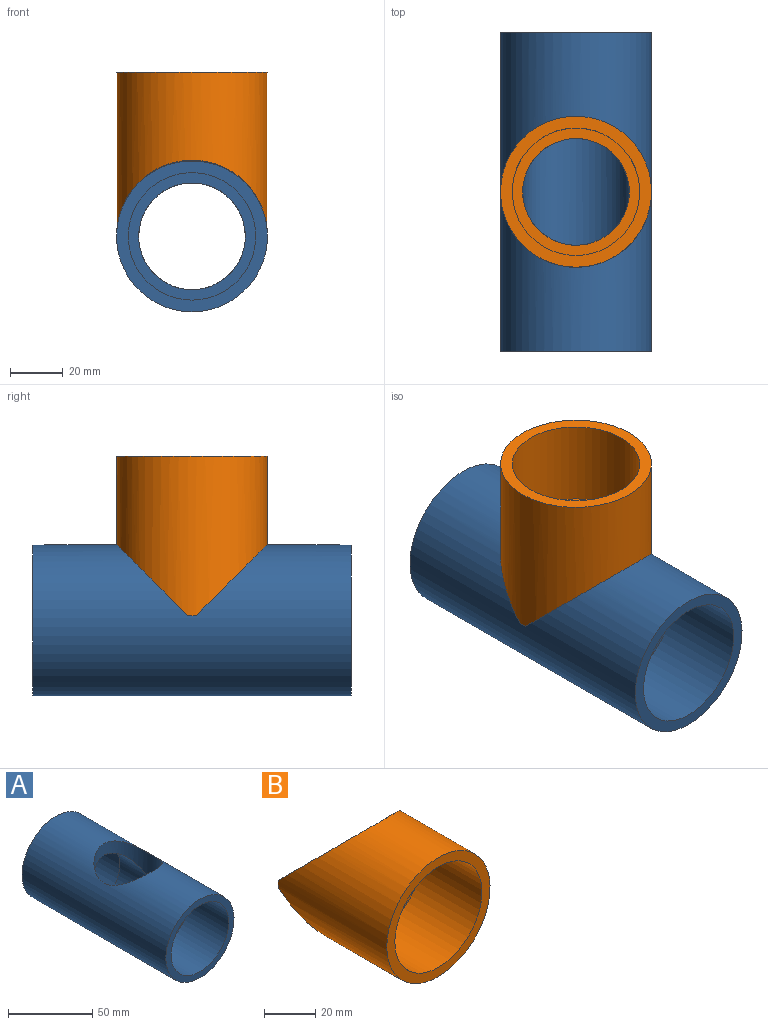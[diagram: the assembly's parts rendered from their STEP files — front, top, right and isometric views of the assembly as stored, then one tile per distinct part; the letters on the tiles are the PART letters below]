
ASSEMBLY  parts=2 mates=1
PART A: 9 faces, bbox 57.2x120.7x57.2 mm
  f0: cylinder r=28.57mm len=120.65mm, axis (0,-1,0), area 20279.6mm2, adj f1,f2,f8
  f1: plane 57.15x57.15mm, normal (0,1,0), area 736mm2, adj f0,f3
  f2: plane 57.15x57.15mm, normal (0,-1,0), area 736mm2, adj f0,f5
  f3: cylinder r=24.13mm len=48.26mm, axis (0,1,0), area 5054.4mm2, adj f1,f4
  f4: plane 48.26x48.26mm, normal (0,1,0), area 548.2mm2, adj f3,f7
  f5: cylinder r=24.13mm len=48.26mm, axis (0,-1,0), area 5054.4mm2, adj f2,f6
  f6: plane 48.26x48.26mm, normal (0,-1,0), area 548.2mm2, adj f5,f7
  f7: cylinder r=20.19mm len=53.98mm, axis (0,-1,0), area 5217.1mm2, adj f4,f6,f8
  f8: cylinder r=20.19mm len=40.39mm, axis (0,0,1), area 1488mm2, adj f0,f7
PART B: 8 faces, bbox 57.2x60.3x57.3 mm
  f0: plane 3.2x0.05mm, normal (0,1,0), area 0.1mm2, adj f2,f7
  f1: cylinder r=20.19mm len=40.39mm, axis (0,1,0), area 508.8mm2, adj f6,f7
  f2: cylinder r=28.57mm len=60.33mm, axis (0,1,0), area 7846.9mm2, adj f0,f3,f4,f7
  f3: plane 57.15x57.15mm, normal (0,-1,0), area 736mm2, adj f2,f5
  f4: plane 3.2x0.05mm, normal (0,1,0), area 0.1mm2, adj f2,f7
  f5: cylinder r=24.13mm len=48.26mm, axis (0,-1,0), area 5054.4mm2, adj f3,f6
  f6: plane 48.26x48.26mm, normal (0,-1,0), area 548.2mm2, adj f1,f5
  f7: cylinder r=28.57mm len=57.33mm, axis (0,0,1), area 1879mm2, adj f0,f1,f2,f4
PLACE A t=(3.9,-44.78,19.94)mm
PLACE B rot(axis=(-1,0,0),90deg) t=(3.9,15.55,21.77)mm
MATE fastened B.f1 <-> A.f8  axis (0,0,1) through (3.9,15.55,48.76)mm
